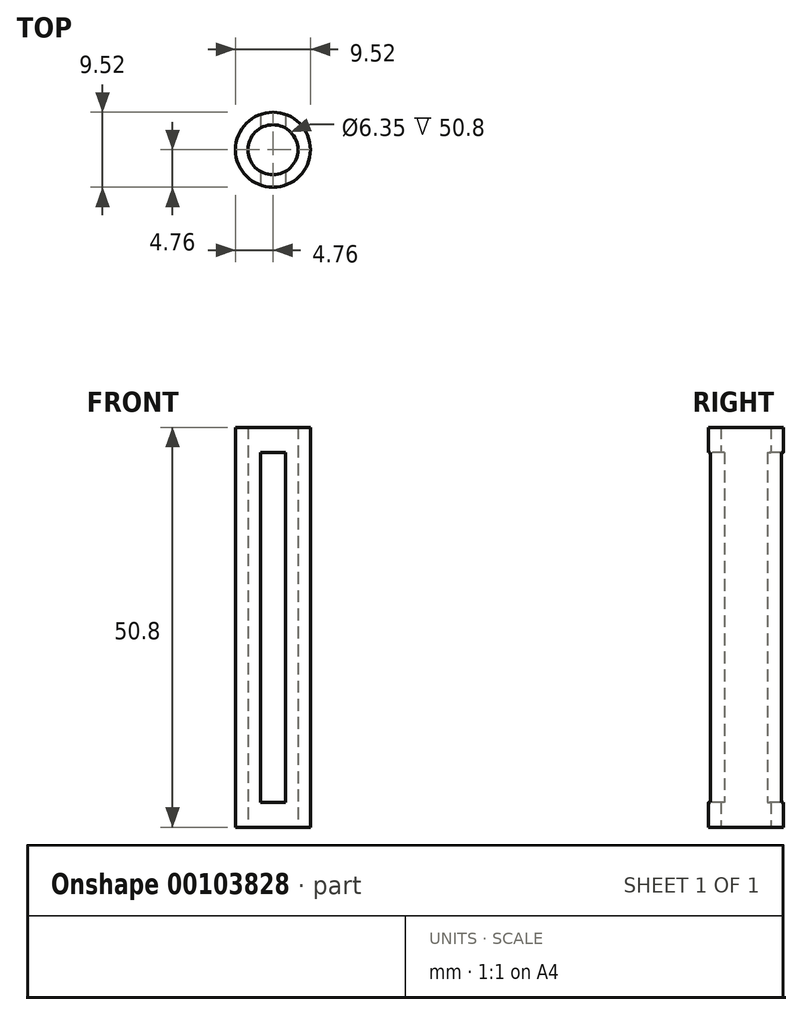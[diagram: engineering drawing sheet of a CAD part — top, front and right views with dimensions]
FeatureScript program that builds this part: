
annotation { "Feature Type Name" : "Feature", "Feature Type Description" : "" }
export const myFeature = defineFeature(function(context is Context, id is Id, definition is map)
    precondition{}
    {
        {
            var Q0;
            Q0=qCreatedBy(makeId("Top.planeOp"),FACE);
            var sketch = newSketch(context, id + "F0", { "sketchPlane" : qUnion([Q0])});
            skCircle(sketch, "E0", {"center": v(0, 0) * mm, "radius": 3.18 * mm});
            skCircle(sketch, "E1", {"center": v(0, 0) * mm, "radius": 4.76 * mm});
            skSolve(sketch);
        }
        {
            var Q0;
            Q0=makeQuery(id+"F0.imprint","IMPRINT",FACE,{"disambiguationData":[TD([[makeQuery(id+"F0.imprint","IMPRINT",EDGE,{"derivedFrom":sQuery(id+"F0.wireOp",EDGE,"E0")}),-1.0]])]});
            extrude(context, id + "F1", {"entities" : qUnion([Q0]), "depth" : 50.8 * mm});
        }
        {
            var Q0;
            Q0=qCreatedBy(makeId("Front.planeOp"),FACE);
            var sketch = newSketch(context, id + "F2", { "sketchPlane" : qUnion([Q0])});
            skLineSegment(sketch, "E2.bottom", {"start": v(1.59, 47.62) * mm, "end": v(-1.59, 47.62) * mm});
            skLineSegment(sketch, "E2.top", {"start": v(1.59, 3.17) * mm, "end": v(-1.59, 3.17) * mm});
            skLineSegment(sketch, "E2.left", {"start": v(1.59, 47.62) * mm, "end": v(1.59, 3.17) * mm});
            skLineSegment(sketch, "E2.right", {"start": v(-1.59, 47.62) * mm, "end": v(-1.59, 3.17) * mm});
            skPoint(sketch, "E2.middle", {"position": v(0, 25.4) * mm});
            skSolve(sketch);
        }
        {
            var Q0;
            Q0 = qSketchRegion(id + "F2", true);
            extrude(context, id + "F3", {"entities" : qUnion([Q0]), "operationType" : NewBodyOperationType.REMOVE, "oppositeDirection" : true, "depth" : 25.4 * mm, "hasSecondDirection" : true, "secondDirectionOppositeDirection" : false, "secondDirectionDepth" : 25.4 * mm});
        }
    });
